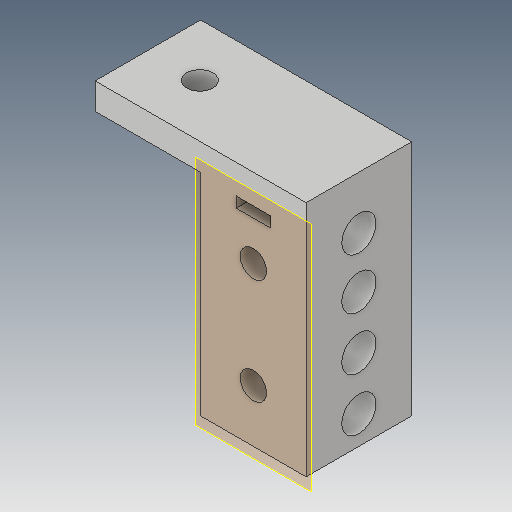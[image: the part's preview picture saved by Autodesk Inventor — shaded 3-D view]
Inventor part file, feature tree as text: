
AUTODESK INVENTOR PART (.ipt)
format: ipt  version: 2019.4 (Build 234330000, 330)  size: 161,280 bytes
history: native  units: mm
features: other x3, sketch x3, plane x2
ambient origin geometry x8: Origin, YZ Plane, XZ Plane, XY Plane, X Axis, Y Axis, Z Axis, Center Point
bodies: Solid1 (feature_tree)
feature tree (8):
  other  "Neje_20mm_rod_connector_double.ipt"
  other  "Solid1::Neje_20mm_rod_connector_double.ipt"
  other  "TaggingFeature1"
  sketch  "Sketch1"  dims[d0=10.0mm]
  sketch  "Sketch2"
  sketch  "Sketch3"
  plane  "Work Plane1"
  plane  "Work Plane2"
